# Revit family: LB_Precast-Console Beam_Spæncom
name_source: partatom
category: Structural Framing
revit_build: Autodesk Revit 2014 (Build: 20130308_1515(x64)
units: mm (PartAtom-declared; Revit-internal decimal feet)

## types (8) — shared parameters
Console thickness = 80 mm  [stored 0.262467 ft]
Height (bjælkekroppen) = 140 mm  [stored 0.459318 ft]
Manufacturer = Spæncom
Width console = 120 mm  [stored 0.393701 ft]

## per-type parameters (varying)
| type | Height element | Width beam top | Width element |
| LB 66/22 | 300 mm | 370 mm  [stored 1.21391 ft] | 660 mm |
| LB 66/27 | 350 mm  [stored 1.14829 ft] | 340 mm  [stored 1.11549 ft] | 660 mm |
| LB 66/32 | 400 mm  [stored 1.31234 ft] | 310 mm  [stored 1.01706 ft] | 660 mm |
| LB 66/40 | 480 mm  [stored 1.5748 ft] | 260 mm  [stored 0.853018 ft] | 660 mm |
| LB 84/22 | 300 mm | 550 mm | 840 mm  [stored 2.75591 ft] |
| LB 84/27 | 350 mm  [stored 1.14829 ft] | 520 mm  [stored 1.70604 ft] | 840 mm  [stored 2.75591 ft] |
| LB 84/32 | 400 mm  [stored 1.31234 ft] | 490 mm  [stored 1.60761 ft] | 840 mm  [stored 2.75591 ft] |
| LB 84/40 | 480 mm  [stored 1.5748 ft] | 440 mm  [stored 1.44357 ft] | 840 mm  [stored 2.75591 ft] |

note: column(s) folded — value = type name in every type: Model

note: [stored X ft] marks values corroborated as IEEE doubles in the binary element streams (Revit-internal decimal feet)

## geometry (parser evidence)
native form markers: Sweep x1
no freeform markers — native parametric forms only
